SOLIDWORKS PART (.sldprt)
format: sldprt  version: not decoded by parser v0  size: 410,112 bytes
history: native  units: mm
features: extrude x59, sketch x1, plane x1 (+10 scaffold rows collapsed)
feature tree (71):
  scaffold x10  (default folders/planes/origin — collapsed)
  sketch  "Sketch1"  dims[c1.D7=10.3124mm c1.D8=10.3124mm c1.D9=10.3124mm c1.D10=10.3124mm c1.D14=10.3124mm c1.D18=28.448mm c1.D19=28.448mm c1.D20=28.448mm c1.D21=28.448mm c1.D22=28.448mm c2.D18=14.224mm c2.D21=14.224mm c2.D19=22.86mm c2.D20=28.448mm c3.D21=22.86mm c3.D18=28.448mm c3.D22=~37.026545mm c3.D20=22.86mm c4.D22=22.86mm c4.D23=~312.928058mm c4.D16=78.74mm c4.D18=~312.928058mm c5.D16=78.74mm c5.D18=78.74mm c5.D23=55.88mm c5.D1=10.3124mm c5.D2=10.3124mm c5.D3=10.3124mm c5.D4=10.3124mm c5.D5=22.86mm c5.D6=22.86mm c5.D7=22.86mm c5.D8=22.86mm c6.D4=10.3124mm c6.D5=22.86mm c6.D18=10.3124mm c6.D10=10.3124mm c6.D16=22.86mm c6.D25=78.74mm c6.D26=107.188mm c6.D27=2.54mm c6.D28=2.54mm c6.D29=53.594mm c7.D28=53.594mm c7.D27=~7.860749mm c7.D5=2.54mm c8.D27=11.43mm c8.D16=10.16mm c8.D5=2.54mm c8.D1=196.85mm c8.D2=88.9mm c8.D3=77.47mm c8.D4=22.86mm c9.D5=63.5mm c9.D6=38.1mm c9.D11=95.25mm c9.D12=120.65mm c9.D13=12.7mm c9.D14=12.7mm c10.D14=~47.123606deg c11.D14=12.7mm c12.D14=45.0deg c12.D15=12.7mm c12.D16=12.7mm c12.D13=12.7mm c12.D17=12.7mm c12.D19=101.6mm c12.D20=14.224mm c12.D18=14.224mm c12.D22=101.6mm c13.D18=12.7mm c13.D13=~70.473173mm c14.D13=45.0deg c14.D14=20.32mm c14.D23=12.7mm c14.D24=12.7mm c14.D17=12.7mm c14.D18=12.7mm c14.D9=88.9mm c14.D10=120.65mm c14.D11=196.85mm c14.D12=95.25mm c15.D13=77.47mm c15.D12=63.5mm c15.D14=22.86mm c15.D15=38.1mm c15.D16=20.32mm c15.D17=120.65mm c16.D17=45.0deg c16.D11=95.25mm c16.D18=196.85mm c16.D10=120.65mm c16.D16=12.7mm c16.D19=12.7mm c17.D16=12.7mm c17.D19=~19.235521mm c17.D7=120.65mm c17.D10=12.7mm c18.D10=90.0deg c18.D19=12.7mm c18.D20=12.7mm c18.D21=12.7mm c18.D22=12.7mm c18.D23=2.54mm c18.D24=20.32mm c18.D25=63.5mm c19.D23=2.54mm c19.D18=~175.82368deg c19.D16=~174.212182deg]
  plane  "Plane1"
  extrude  "Extrude1"  Depth=6.35mm cosMaterialEX=10009317
  extrude  "sMaterialName"  [1 undecoded]
  extrude  "cosFMVItemName"  [1 undecoded]
  extrude  "cosMaterialName"  [1 undecoded]
  extrude  "cosComponentName"  [1 undecoded]
  extrude  "cosMaterialType"  [1 undecoded]
  extrude  "cosMaterialLibFile"  [1 undecoded]
  extrude  "cosMaterialRefPlaneName"  [1 undecoded]
  extrude  "sMaterialSourceName"  [1 undecoded]
  extrude  "sMaterialName"  [1 undecoded]
  extrude  "cosFMVItemName"  [1 undecoded]
  extrude  "cosMaterialName"  [1 undecoded]
  extrude  "cosComponentName"  [1 undecoded]
  extrude  "cosMaterialType"  [1 undecoded]
  extrude  "cosMaterialLibFile"  [1 undecoded]
  extrude  "cosMaterialRefPlaneName"  [1 undecoded]
  extrude  "cosForceRefPlaneName"  [1 undecoded]
  extrude  "cosFMVItemName"  [1 undecoded]
  extrude  "cosDistributionCoordSysName"  [1 undecoded]
  extrude  "cosLBCSymbolColor"  Depth=0 cosForce7=0
  extrude  "cosForceRefPlaneName"  [1 undecoded]
  extrude  "cosFMVItemName"  [1 undecoded]
  extrude  "cosDistributionCoordSysName"  [1 undecoded]
  extrude  "cosLBCSymbolColor"  [1 undecoded]
  extrude  "cosForceRefPlaneName"  [1 undecoded]
  extrude  "cosFMVItemName"  [1 undecoded]
  extrude  "cosDistributionCoordSysName"  [1 undecoded]
  extrude  "cosLBCSymbolColor"  [1 undecoded]
  extrude  "cosRestraintRefPlaneName"  [1 undecoded]
  extrude  "cosFMVItemName"  [1 undecoded]
  extrude  "cosLBCSymbolColor"  Depth=0 cosRestraint7=0
  extrude  "cosRestraintRefPlaneName"  [1 undecoded]
  extrude  "cosFMVItemName"  [1 undecoded]
  extrude  "cosLBCSymbolColor"  [1 undecoded]
  extrude  "cosRestraintRefPlaneName"  [1 undecoded]
  extrude  "cosFMVItemName"  [1 undecoded]
  extrude  "cosLBCSymbolColor"  Depth=0 cosFaceID=0
  extrude  "sMaterialSourceName"  [1 undecoded]
  extrude  "sMaterialName"  [1 undecoded]
  extrude  "cosFMVItemName"  [1 undecoded]
  extrude  "cosMaterialName"  [1 undecoded]
  extrude  "cosComponentName"  [1 undecoded]
  extrude  "cosMaterialType"  [1 undecoded]
  extrude  "cosMaterialLibFile"  [1 undecoded]
  extrude  "cosMaterialRefPlaneName"  [1 undecoded]
  extrude  "cosForceRefPlaneName"  [1 undecoded]
  extrude  "cosFMVItemName"  [1 undecoded]
  extrude  "cosDistributionCoordSysName"  [1 undecoded]
  extrude  "cosLBCSymbolColor"  [1 undecoded]
  extrude  "cosForceRefPlaneName"  [1 undecoded]
  extrude  "cosFMVItemName"  [1 undecoded]
  extrude  "cosDistributionCoordSysName"  [1 undecoded]
  extrude  "cosLBCSymbolColor"  [1 undecoded]
  extrude  "cosRestraintRefPlaneName"  [1 undecoded]
  extrude  "cosFMVItemName"  [1 undecoded]
  extrude  "cosLBCSymbolColor"  [1 undecoded]
  extrude  "cosRestraintRefPlaneName"  [1 undecoded]
  extrude  "cosFMVItemName"  [1 undecoded]
  extrude  "cosLBCSymbolColor"  [1 undecoded]
decode coverage: 5 of 60 modeling features carry decoded parameters
note: ~ marks probable driven/reference dimensions
note: 55 parameter values undecoded
summary: no parameter record found for 55 features
note: suppression state not decoded; provenance and decode notes live in map.json
